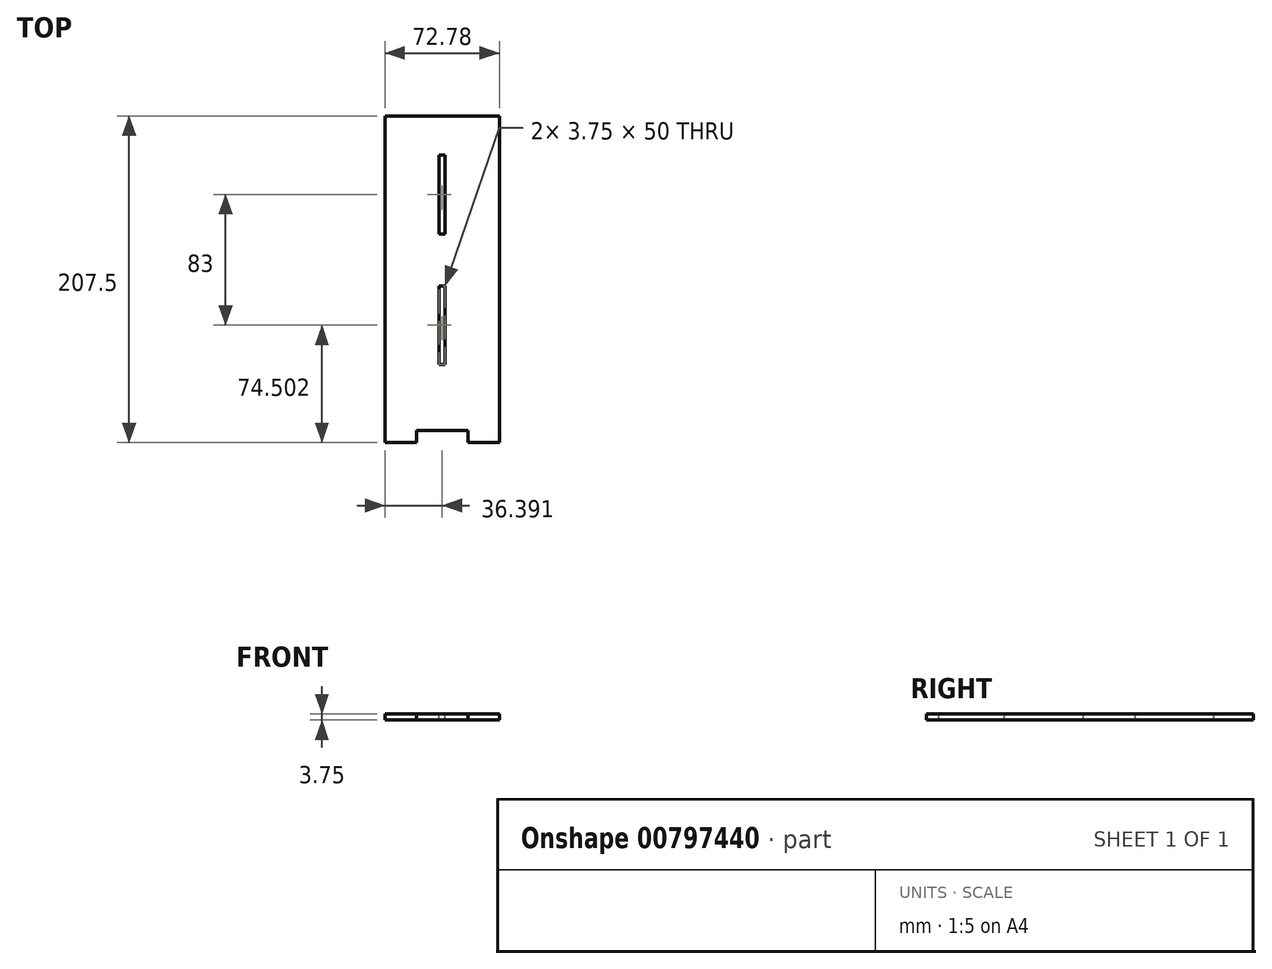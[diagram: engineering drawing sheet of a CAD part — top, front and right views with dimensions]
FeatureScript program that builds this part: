
annotation { "Feature Type Name" : "Feature", "Feature Type Description" : "" }
export const myFeature = defineFeature(function(context is Context, id is Id, definition is map)
    precondition{}
    {
        {
            var Q0;
            Q0=qCreatedBy(makeId("Top.planeOp"),FACE);
            var sketch = newSketch(context, id + "F0", { "sketchPlane" : qUnion([Q0])});
            skLineSegment(sketch, "E0.bottom", {"start": v(20, -16.18) * mm, "end": v(52.78, -16.18) * mm});
            skLineSegment(sketch, "E0.top", {"start": v(0, 183.82) * mm, "end": v(72.78, 183.82) * mm});
            skLineSegment(sketch, "E0.left", {"start": v(0, -16.18) * mm, "end": v(0, 183.82) * mm});
            skLineSegment(sketch, "E0.right", {"start": v(72.78, -16.18) * mm, "end": v(72.78, 183.82) * mm});
            skLineSegment(sketch, "E1.top", {"start": v(0, -23.68) * mm, "end": v(20, -23.68) * mm});
            skLineSegment(sketch, "E1.left", {"start": v(0, -16.18) * mm, "end": v(0, -23.68) * mm});
            skLineSegment(sketch, "E1.right", {"start": v(20, -16.18) * mm, "end": v(20, -23.68) * mm});
            skLineSegment(sketch, "E2.top", {"start": v(72.78, -23.68) * mm, "end": v(52.78, -23.68) * mm});
            skLineSegment(sketch, "E2.left", {"start": v(72.78, -16.18) * mm, "end": v(72.78, -23.68) * mm});
            skLineSegment(sketch, "E2.right", {"start": v(52.78, -16.18) * mm, "end": v(52.78, -23.68) * mm});
            skSolve(sketch);
        }
        {
            var Q0;
            Q0=makeQuery(id+"F0.imprint","IMPRINT",FACE,{"disambiguationData":[TD([[makeQuery(id+"F0.imprint","IMPRINT",EDGE,{"derivedFrom":sQuery(id+"F0.wireOp",EDGE,"E0.bottom")}),1.0]])]});
            extrude(context, id + "F1", {"entities" : qUnion([Q0]), "depth" : 3.75 * mm, "offsetDistance" : 25 * mm});
        }
        {
            var Q0;
            Q0=makeQuery(id+"F1.opExtrude","CAP_FACE",FACE,{"disambiguationData":[OSD([sQuery(id+"F0.wireOp",EDGE,"E0.bottom"),sQuery(id+"F0.wireOp",EDGE,"E0.top"),sQuery(id+"F0.wireOp",EDGE,"E0.left"),sQuery(id+"F0.wireOp",EDGE,"E0.right"),sQuery(id+"F0.wireOp",EDGE,"E1.top"),sQuery(id+"F0.wireOp",EDGE,"E1.left"),sQuery(id+"F0.wireOp",EDGE,"E1.right"),sQuery(id+"F0.wireOp",EDGE,"E2.top"),sQuery(id+"F0.wireOp",EDGE,"E2.left"),sQuery(id+"F0.wireOp",EDGE,"E2.right")])],"isStart":false});
            var sketch = newSketch(context, id + "F2", { "sketchPlane" : qUnion([Q0])});
            skLineSegment(sketch, "E3.bottom", {"start": v(34.52, 158.82) * mm, "end": v(38.27, 158.82) * mm});
            skLineSegment(sketch, "E3.top", {"start": v(34.52, 108.82) * mm, "end": v(38.27, 108.82) * mm});
            skLineSegment(sketch, "E3.left", {"start": v(34.52, 158.82) * mm, "end": v(34.52, 108.82) * mm});
            skLineSegment(sketch, "E3.right", {"start": v(38.27, 158.82) * mm, "end": v(38.27, 108.82) * mm});
            skLineSegment(sketch, "E4.bottom", {"start": v(34.52, 75.82) * mm, "end": v(38.27, 75.82) * mm});
            skLineSegment(sketch, "E4.top", {"start": v(34.52, 25.82) * mm, "end": v(38.27, 25.82) * mm});
            skLineSegment(sketch, "E4.left", {"start": v(34.52, 75.82) * mm, "end": v(34.52, 25.82) * mm});
            skLineSegment(sketch, "E4.right", {"start": v(38.27, 75.82) * mm, "end": v(38.27, 25.82) * mm});
            skSolve(sketch);
        }
        {
            var Q0;
            Q0=makeQuery(id+"F2.imprint","IMPRINT",FACE,{"disambiguationData":[TD([[makeQuery(id+"F2.imprint","IMPRINT",EDGE,{"derivedFrom":sQuery(id+"F2.wireOp",EDGE,"E4.bottom")}),-1.0]])]});
            var Q1;
            Q1=makeQuery(id+"F2.imprint","IMPRINT",FACE,{"disambiguationData":[TD([[makeQuery(id+"F2.imprint","IMPRINT",EDGE,{"derivedFrom":sQuery(id+"F2.wireOp",EDGE,"E3.bottom")}),-1.0]])]});
            extrude(context, id + "F3", {"entities" : qUnion([Q0, Q1]), "operationType" : NewBodyOperationType.REMOVE, "oppositeDirection" : true, "depth" : 3.75 * mm, "offsetDistance" : 25 * mm});
        }
    });
